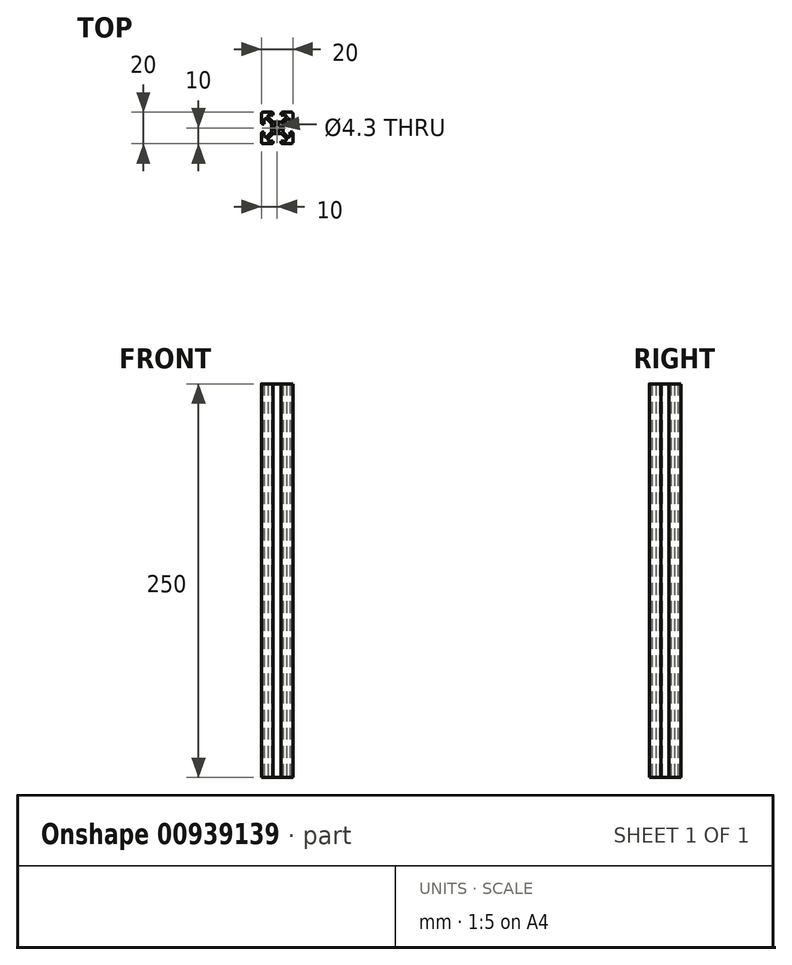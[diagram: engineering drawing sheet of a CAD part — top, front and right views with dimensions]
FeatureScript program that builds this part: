
annotation { "Feature Type Name" : "Feature", "Feature Type Description" : "" }
export const myFeature = defineFeature(function(context is Context, id is Id, definition is map)
    precondition{}
    {
        {
            var Q0;
            Q0=qCreatedBy(makeId("Top.planeOp"),FACE);
            var sketch = newSketch(context, id + "F0", { "sketchPlane" : qUnion([Q0]) });
            skArc(sketch, "E0", {"start": v(10, 9) * mm, "mid": v(9.7, 9.7) * mm, "end": v(9, 10) * mm});
            skArc(sketch, "E1", {"start": v(-9, 10) * mm, "mid": v(-9.7, 9.7) * mm, "end": v(-10, 9) * mm});
            skArc(sketch, "E2", {"start": v(-10, -9) * mm, "mid": v(-9.7, -9.7) * mm, "end": v(-9, -10) * mm});
            skArc(sketch, "E3", {"start": v(9, -10) * mm, "mid": v(9.7, -9.7) * mm, "end": v(10, -9) * mm});
            skLineSegment(sketch, "E4", {"start": v(3.5, 10) * mm, "end": v(9, 10) * mm});
            skLineSegment(sketch, "E5", {"start": v(-9, 10) * mm, "end": v(-3.5, 10) * mm});
            skLineSegment(sketch, "E6", {"start": v(8.2, 2.5) * mm, "end": v(9, 2.5) * mm});
            skLineSegment(sketch, "E7", {"start": v(-9, 2.5) * mm, "end": v(-8.2, 2.5) * mm});
            skLineSegment(sketch, "E8", {"start": v(8.2, -2.5) * mm, "end": v(9, -2.5) * mm});
            skLineSegment(sketch, "E9", {"start": v(-9, -2.5) * mm, "end": v(-8.2, -2.5) * mm});
            skLineSegment(sketch, "E10", {"start": v(3.5, -10) * mm, "end": v(9, -10) * mm});
            skLineSegment(sketch, "E11", {"start": v(-9, -10) * mm, "end": v(-3.5, -10) * mm});
            skLineSegment(sketch, "E12", {"start": v(-10, -3.5) * mm, "end": v(-10, -9) * mm});
            skLineSegment(sketch, "E13", {"start": v(-10, 9) * mm, "end": v(-10, 3.5) * mm});
            skLineSegment(sketch, "E14", {"start": v(-2.5, -8.2) * mm, "end": v(-2.5, -9) * mm});
            skLineSegment(sketch, "E15", {"start": v(-2.5, 9) * mm, "end": v(-2.5, 8.2) * mm});
            skLineSegment(sketch, "E16", {"start": v(2.5, -8.2) * mm, "end": v(2.5, -9) * mm});
            skLineSegment(sketch, "E17", {"start": v(2.5, 9) * mm, "end": v(2.5, 8.2) * mm});
            skLineSegment(sketch, "E18", {"start": v(10, 3.5) * mm, "end": v(10, 9) * mm});
            skLineSegment(sketch, "E19", {"start": v(10, -9) * mm, "end": v(10, -3.5) * mm});
            skArc(sketch, "E20", {"start": v(-2.5, 9) * mm, "mid": v(-2.8, 9.7) * mm, "end": v(-3.5, 10) * mm});
            skArc(sketch, "E21", {"start": v(3.5, 10) * mm, "mid": v(2.8, 9.7) * mm, "end": v(2.5, 9) * mm});
            skArc(sketch, "E22", {"start": v(9, 2.5) * mm, "mid": v(9.7, 2.8) * mm, "end": v(10, 3.5) * mm});
            skArc(sketch, "E23", {"start": v(10, -3.5) * mm, "mid": v(9.7, -2.8) * mm, "end": v(9, -2.5) * mm});
            skArc(sketch, "E24", {"start": v(2.5, -9) * mm, "mid": v(2.8, -9.7) * mm, "end": v(3.5, -10) * mm});
            skArc(sketch, "E25", {"start": v(-3.5, -10) * mm, "mid": v(-2.8, -9.7) * mm, "end": v(-2.5, -9) * mm});
            skArc(sketch, "E26", {"start": v(-9, -2.5) * mm, "mid": v(-9.7, -2.8) * mm, "end": v(-10, -3.5) * mm});
            skLineSegment(sketch, "E27", {"start": v(2.5, -8.2) * mm, "end": v(4.9, -8.2) * mm});
            skLineSegment(sketch, "E28", {"start": v(8.2, -4.9) * mm, "end": v(8.2, -2.5) * mm});
            skLineSegment(sketch, "E29", {"start": v(8.2, 2.5) * mm, "end": v(8.2, 4.9) * mm});
            skLineSegment(sketch, "E30", {"start": v(2.5, 8.2) * mm, "end": v(4.9, 8.2) * mm});
            skLineSegment(sketch, "E31", {"start": v(-4.9, 8.2) * mm, "end": v(-2.5, 8.2) * mm});
            skLineSegment(sketch, "E32", {"start": v(-8.2, 4.9) * mm, "end": v(-8.2, 2.5) * mm});
            skLineSegment(sketch, "E33", {"start": v(-8.2, -2.5) * mm, "end": v(-8.2, -4.9) * mm});
            skLineSegment(sketch, "E34", {"start": v(-4.9, -8.2) * mm, "end": v(-2.5, -8.2) * mm});
            skArc(sketch, "E35", {"start": v(-10, 3.5) * mm, "mid": v(-9.7, 2.8) * mm, "end": v(-9, 2.5) * mm});
            skLineSegment(sketch, "E36", {"start": v(3.94, -3.06) * mm, "end": v(6.5, -5.6) * mm});
            skLineSegment(sketch, "E37", {"start": v(-5.6, 6.5) * mm, "end": v(-3.06, 3.94) * mm});
            skLineSegment(sketch, "E38", {"start": v(3.06, -3.94) * mm, "end": v(5.6, -6.5) * mm});
            skLineSegment(sketch, "E39", {"start": v(-6.5, 5.6) * mm, "end": v(-3.94, 3.06) * mm});
            skLineSegment(sketch, "E40", {"start": v(-3.94, -3.06) * mm, "end": v(-6.5, -5.6) * mm});
            skLineSegment(sketch, "E41", {"start": v(5.6, 6.5) * mm, "end": v(3.06, 3.94) * mm});
            skLineSegment(sketch, "E42", {"start": v(3.94, 3.06) * mm, "end": v(6.5, 5.6) * mm});
            skLineSegment(sketch, "E43", {"start": v(-5.6, -6.5) * mm, "end": v(-3.06, -3.94) * mm});
            skLineSegment(sketch, "E44", {"start": v(-3.65, 2.35) * mm, "end": v(-3.65, -2.35) * mm});
            skLineSegment(sketch, "E45", {"start": v(3.65, -2.35) * mm, "end": v(3.65, 2.35) * mm});
            skArc(sketch, "E46", {"start": v(3.65, -2.35) * mm, "mid": v(3.73, -2.73) * mm, "end": v(3.94, -3.06) * mm});
            skArc(sketch, "E47", {"start": v(3.94, 3.06) * mm, "mid": v(3.73, 2.73) * mm, "end": v(3.65, 2.35) * mm});
            skArc(sketch, "E48", {"start": v(-3.94, -3.06) * mm, "mid": v(-3.73, -2.73) * mm, "end": v(-3.65, -2.35) * mm});
            skArc(sketch, "E49", {"start": v(-3.65, 2.35) * mm, "mid": v(-3.73, 2.73) * mm, "end": v(-3.94, 3.06) * mm});
            skLineSegment(sketch, "E50", {"start": v(-2.35, 3.65) * mm, "end": v(2.35, 3.65) * mm});
            skLineSegment(sketch, "E51", {"start": v(-2.35, -3.65) * mm, "end": v(2.35, -3.65) * mm});
            skArc(sketch, "E52", {"start": v(3.06, -3.94) * mm, "mid": v(2.73, -3.73) * mm, "end": v(2.35, -3.65) * mm});
            skArc(sketch, "E53", {"start": v(2.35, 3.65) * mm, "mid": v(2.73, 3.73) * mm, "end": v(3.06, 3.94) * mm});
            skArc(sketch, "E54", {"start": v(-2.35, -3.65) * mm, "mid": v(-2.73, -3.73) * mm, "end": v(-3.06, -3.94) * mm});
            skArc(sketch, "E55", {"start": v(-3.06, 3.94) * mm, "mid": v(-2.73, 3.73) * mm, "end": v(-2.35, 3.65) * mm});
            skArc(sketch, "E56", {"start": v(-6.5, 5.6) * mm, "mid": v(-7.58, 5.82) * mm, "end": v(-8.2, 4.9) * mm});
            skArc(sketch, "E57", {"start": v(-4.9, 8.2) * mm, "mid": v(-5.82, 7.58) * mm, "end": v(-5.6, 6.5) * mm});
            skArc(sketch, "E58", {"start": v(5.6, 6.5) * mm, "mid": v(5.82, 7.58) * mm, "end": v(4.9, 8.2) * mm});
            skArc(sketch, "E59", {"start": v(8.2, 4.9) * mm, "mid": v(7.58, 5.82) * mm, "end": v(6.5, 5.6) * mm});
            skArc(sketch, "E60", {"start": v(6.5, -5.6) * mm, "mid": v(7.58, -5.82) * mm, "end": v(8.2, -4.9) * mm});
            skArc(sketch, "E61", {"start": v(4.9, -8.2) * mm, "mid": v(5.82, -7.58) * mm, "end": v(5.6, -6.5) * mm});
            skArc(sketch, "E62", {"start": v(-5.6, -6.5) * mm, "mid": v(-5.82, -7.58) * mm, "end": v(-4.9, -8.2) * mm});
            skArc(sketch, "E63", {"start": v(-8.2, -4.9) * mm, "mid": v(-7.58, -5.82) * mm, "end": v(-6.5, -5.6) * mm});
            skCircle(sketch, "E64", {"center": v(0, 0) * mm, "radius": 2.15 * mm});
            skSolve(sketch);
        }
        {
            var Q0;
            Q0=makeQuery(id+"F0.imprint","IMPRINT",FACE,{"disambiguationData":[TD([[makeQuery(id+"F0.imprint","IMPRINT",EDGE,{"derivedFrom":sQuery(id+"F0.wireOp",EDGE,"E0")}),1.0]])]});
            extrude(context, id + "F1", {"entities" : qUnion([Q0]), "depth" : 250 * mm, "offsetDistance" : 25 * mm});
        }
    });
